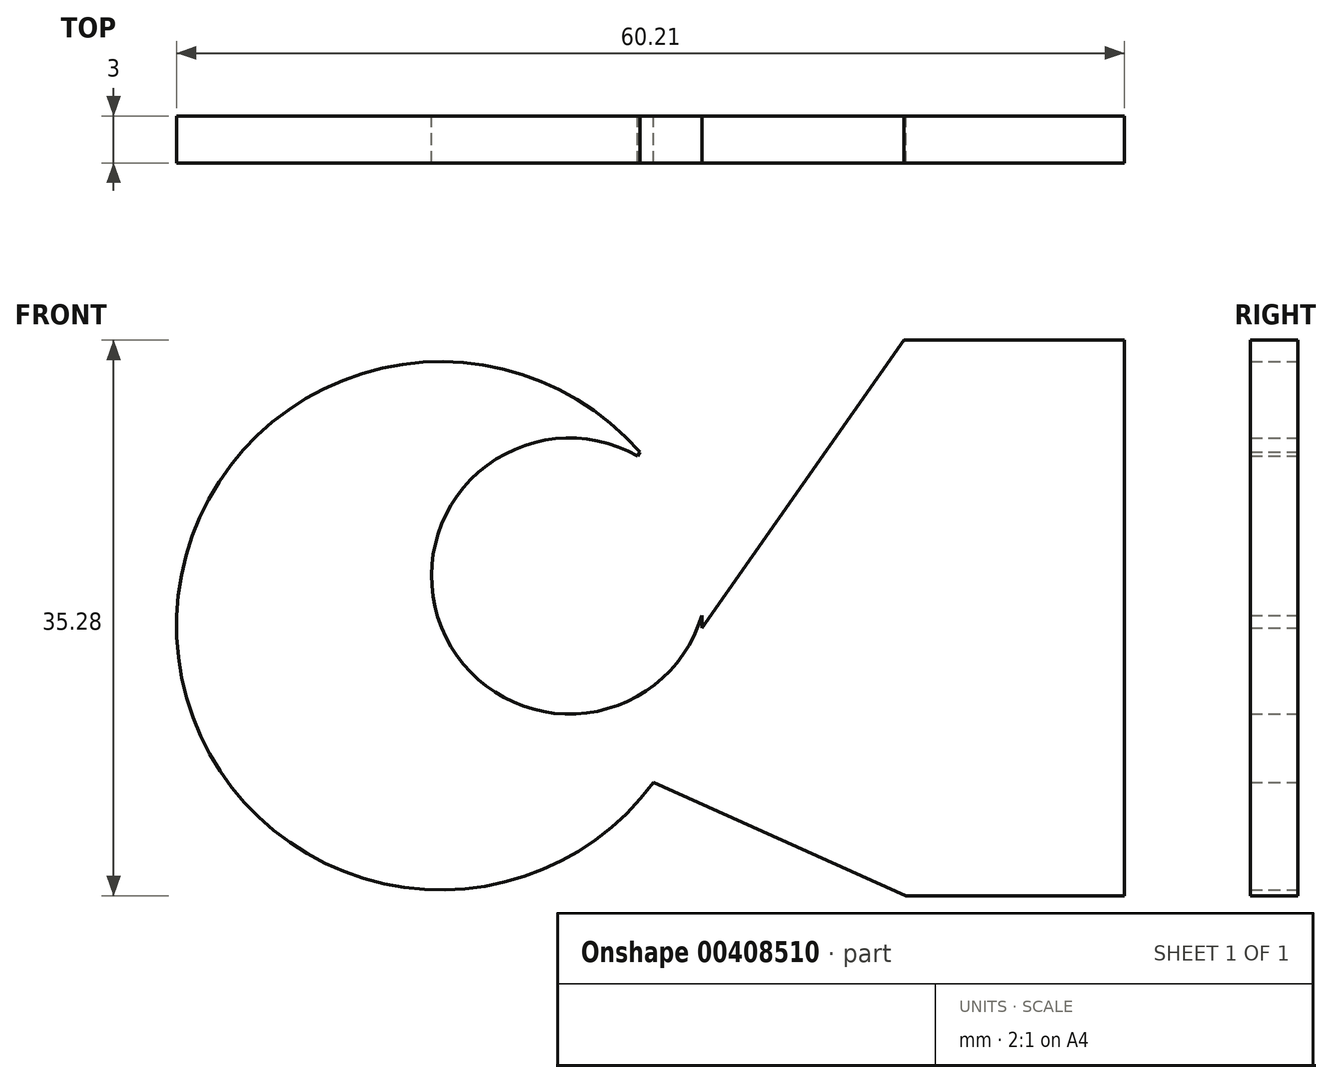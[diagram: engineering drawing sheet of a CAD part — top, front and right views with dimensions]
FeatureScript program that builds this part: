
annotation { "Feature Type Name" : "Feature", "Feature Type Description" : "" }
export const myFeature = defineFeature(function(context is Context, id is Id, definition is map)
    precondition{}
    {
        {
            var Q0;
            Q0=qCreatedBy(makeId("Front.planeOp"),FACE);
            var sketch = newSketch(context, id + "F0", { "sketchPlane" : qUnion([Q0])});
            skLineSegment(sketch, "E0", {"start": v(0, 29.92) * mm, "end": v(-14, 29.92) * mm});
            skLineSegment(sketch, "E1", {"start": v(-14, 29.92) * mm, "end": v(-27.26, 11.05) * mm});
            skArc(sketch, "E2", {"start": v(-30.72, 22.45) * mm, "mid": v(-43.43, 11.78) * mm, "end": v(-26.85, 12.42) * mm});
            skArc(sketch, "E3", {"start": v(-26.84, 11.66) * mm, "mid": v(-26.84, 12.04) * mm, "end": v(-26.85, 12.42) * mm});
            skLineSegment(sketch, "E4", {"start": v(0, 29.92) * mm, "end": v(0, -5.36) * mm});
            skLineSegment(sketch, "E5", {"start": v(0, -5.36) * mm, "end": v(-13.88, -5.36) * mm});
            skLineSegment(sketch, "E6", {"start": v(-13.88, -5.36) * mm, "end": v(-30.09, 1.92) * mm});
            skArc(sketch, "E7", {"start": v(-30.78, 22.82) * mm, "mid": v(-60.2, 11.08) * mm, "end": v(-29.9, 1.84) * mm});
            skLineSegment(sketch, "E8", {"start": v(-30.92, 22.57) * mm, "end": v(-30.78, 22.82) * mm});
            skSolve(sketch);
        }
        {
            var Q0;
            Q0 = qSketchRegion(id + "F0", true);
            var Q1;
            {var subQ4=sQuery(id+"F0.wireOp",EDGE,"E0");Q1=makeQuery(id+"F0.imprint","IMPRINT",FACE,{"disambiguationData":[TD([[makeQuery(id+"F0.imprint","IMPRINT",EDGE,{"derivedFrom":subQ4}),1.0]])]});}
            extrude(context, id + "F1", {"entities" : qUnion([Q0, Q1]), "depth" : 3 * mm});
        }
    });
